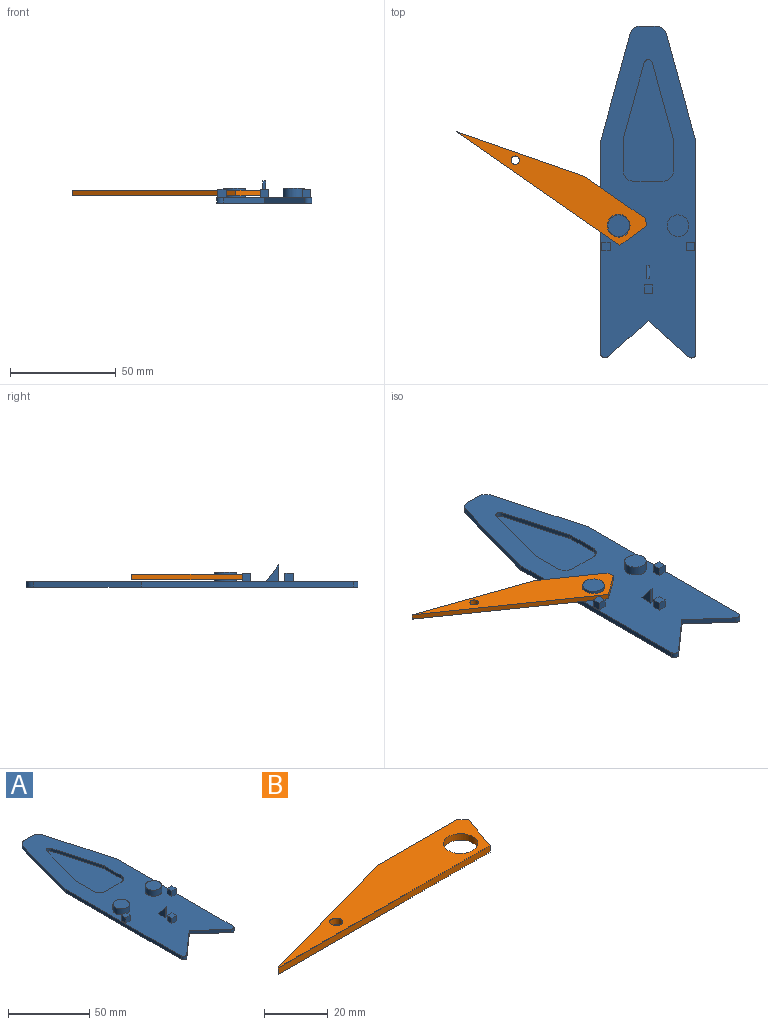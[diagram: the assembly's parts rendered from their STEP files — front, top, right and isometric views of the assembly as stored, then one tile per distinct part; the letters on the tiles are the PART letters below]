
ASSEMBLY  parts=2 mates=1
PART A: 47 faces, bbox 45x157x10.5 mm
  f0: plane 156.96x45mm, normal (0,0,1), area 4711.6mm2, adj f1,f2,f3,f4,f5,f6,f7,f8
  f1: plane 100.55x2.5mm, normal (-1,0,0), area 251.4mm2, adj f0,f2,f11,f12
  f2: cylinder r=2mm len=3.33mm, axis (0,0,-1), area 11.5mm2, adj f0,f1,f3,f12
  f3: plane 19.17x17.04mm, normal (0.66,-0.75,0), area 64.1mm2, adj f0,f2,f4,f12
  f4: plane 19.17x17.04mm, normal (-0.66,-0.75,0), area 64.1mm2, adj f0,f3,f5,f12
  f5: cylinder r=2mm len=3.33mm, axis (0,0,-1), area 11.5mm2, adj f0,f4,f6,f12
  f6: plane 100.55x2.5mm, normal (1,0,0), area 251.4mm2, adj f0,f5,f7,f12
  f7: plane 50.74x13.99mm, normal (0.96,0.27,0), area 131.6mm2, adj f0,f6,f8,f12
  f8: cylinder r=5mm len=4.82mm, axis (0,0,-1), area 16.3mm2, adj f0,f7,f9,f12
  f9: plane 7.38x2.5mm, normal (0,1,0), area 18.5mm2, adj f0,f8,f10,f12
  f10: cylinder r=5mm len=4.82mm, axis (0,0,-1), area 16.3mm2, adj f0,f9,f11,f12
  f11: plane 50.74x13.99mm, normal (-0.96,0.27,0), area 131.6mm2, adj f0,f1,f10,f12
  f12: plane 156.96x45mm, normal (0,0,-1), area 5893.3mm2, adj f1,f2,f3,f4,f5,f6,f7,f8
  f13: cylinder r=5.09mm len=10.18mm, axis (0,0,-1), area 143.9mm2, adj f0,f14
  f14: plane 10.18x10.18mm, normal (0,0,1), area 81.4mm2, adj f13
  f15: cylinder r=5.09mm len=10.18mm, axis (0,0,-1), area 143.9mm2, adj f0,f16
  f16: plane 10.18x10.18mm, normal (0,0,1), area 81.4mm2, adj f15
  f17: plane 4x4mm, normal (-1,0,0), area 16mm2, adj f0,f18,f20,f21
  f18: plane 4x4mm, normal (0,-1,0), area 16mm2, adj f0,f17,f19,f21
  f19: plane 4x4mm, normal (1,0,0), area 16mm2, adj f0,f18,f20,f21
  f20: plane 4x4mm, normal (0,1,0), area 16mm2, adj f0,f17,f19,f21
  f21: plane 4x4mm, normal (0,0,1), area 16mm2, adj f17,f18,f19,f20
  f22: plane 4x4mm, normal (-1,0,0), area 16mm2, adj f0,f23,f25,f26
  f23: plane 4x4mm, normal (0,-1,0), area 16mm2, adj f0,f22,f24,f26
  f24: plane 4x4mm, normal (1,0,0), area 16mm2, adj f0,f23,f25,f26
  f25: plane 4x4mm, normal (0,1,0), area 16mm2, adj f0,f22,f24,f26
  f26: plane 4x4mm, normal (0,0,1), area 16mm2, adj f22,f23,f24,f25
  f27: plane 4x4mm, normal (0,-1,0), area 16mm2, adj f0,f28,f30,f31
  f28: plane 4x4mm, normal (1,0,0), area 16mm2, adj f0,f27,f29,f31
  f29: plane 4x4mm, normal (0,1,0), area 16mm2, adj f0,f28,f30,f31
  f30: plane 4x4mm, normal (-1,0,0), area 16mm2, adj f0,f27,f29,f31
  f31: plane 4x4mm, normal (0,0,1), area 16mm2, adj f27,f28,f29,f30
  f32: plane 13.7x2.2mm, normal (0,1,0), area 30.1mm2, adj f0,f33,f41,f42
  f33: cylinder r=5mm len=5mm, axis (0,0,1), area 17.3mm2, adj f0,f32,f34,f42
  f34: plane 14.32x2.2mm, normal (-1,0,0), area 31.5mm2, adj f0,f33,f35,f42
  f35: cylinder r=5mm len=2.2mm, axis (0,0,1), area 3mm2, adj f0,f34,f36,f42
  f36: plane 35.35x9.74mm, normal (-0.96,-0.27,0), area 80.7mm2, adj f0,f35,f37,f42
  f37: cylinder r=2mm len=3.86mm, axis (0,0,1), area 11.5mm2, adj f0,f36,f38,f42
  f38: plane 35.35x9.74mm, normal (0.96,-0.27,0), area 80.7mm2, adj f0,f37,f39,f42
  f39: cylinder r=5mm len=2.2mm, axis (0,0,1), area 3mm2, adj f0,f38,f40,f42
  f40: plane 14.32x2.2mm, normal (1,0,0), area 31.5mm2, adj f0,f39,f41,f42
  f41: cylinder r=5mm len=5mm, axis (0,0,1), area 17.3mm2, adj f0,f32,f40,f42
  f42: plane 57.47x23.7mm, normal (0,0,1), area 963.5mm2, adj f32,f33,f34,f35,f36,f37,f38,f39
  f43: plane 8x6mm, normal (0,0.8,0.6), area 12.5mm2, adj f0,f44,f45,f46
  f44: plane 8x1.25mm, normal (0,-1,0), area 10mm2, adj f0,f43,f45,f46
  f45: plane 8x6mm, normal (1,0,0), area 24mm2, adj f0,f43,f44
  f46: plane 8x6mm, normal (-1,0,0), area 24mm2, adj f0,f43,f44
PART B: 9 faces, bbox 99.4x17.3x2.5 mm
  f0: plane 2.71x2.51mm, normal (0.68,0.73,0), area 9.2mm2, adj f1,f4,f7,f8
  f1: plane 34.69x2.5mm, normal (0,1,0), area 86.7mm2, adj f0,f2,f7,f8
  f2: plane 62.03x17.3mm, normal (-0.27,0.96,0), area 161mm2, adj f1,f3,f7,f8
  f3: plane 94.23x2.5mm, normal (0,-1,0), area 235.6mm2, adj f2,f4,f7,f8
  f4: plane 14.79x5.21mm, normal (0.94,-0.33,0), area 39.2mm2, adj f0,f3,f7,f8
  f5: cylinder r=5.39mm len=10.78mm, axis (0,0,-1), area 84.6mm2, adj f7,f8
  f6: cylinder r=2mm len=4mm, axis (0,0,-1), area 31.4mm2, adj f7,f8
  f7: plane 99.44x17.3mm, normal (0,0,1), area 1038mm2, adj f0,f1,f2,f3,f4,f5,f6
  f8: plane 99.44x17.3mm, normal (0,0,-1), area 1038mm2, adj f0,f1,f2,f3,f4,f5,f6
PLACE A t=(-51.78,-60.64,32.16)mm fixed
PLACE B rot(axis=(0,0,-1),34.8deg) t=(-75.42,-76.1,33.16)mm
MATE revolute B.f5 <-> A.f13  axis (0,0,-1) through (-88.28,-30.64,36.91)mm
